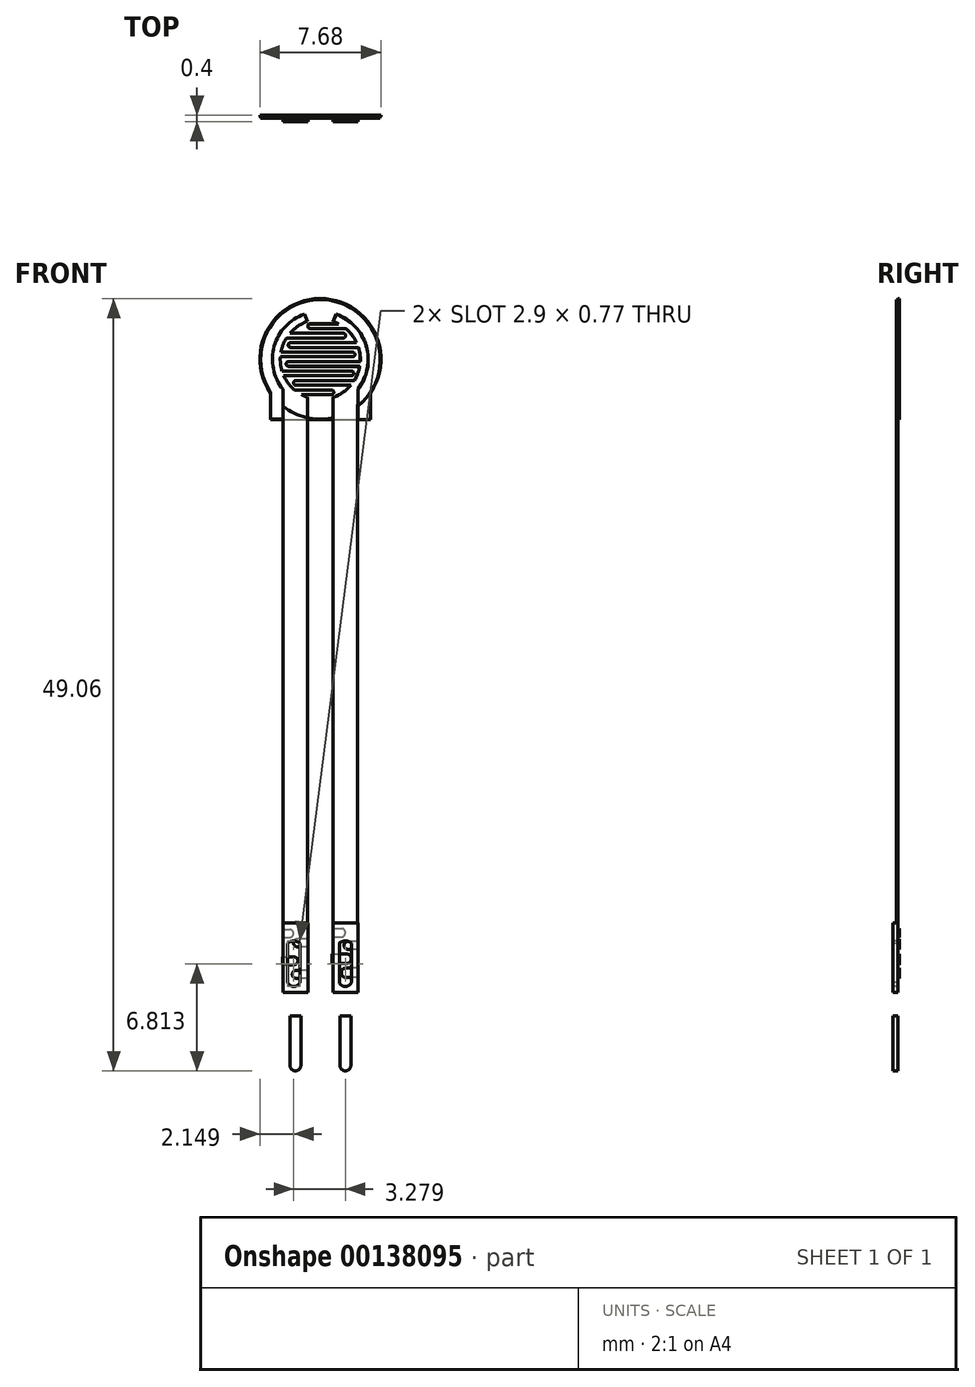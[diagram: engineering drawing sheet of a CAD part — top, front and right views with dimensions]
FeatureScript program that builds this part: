
annotation { "Feature Type Name" : "Feature", "Feature Type Description" : "" }
export const myFeature = defineFeature(function(context is Context, id is Id, definition is map)
    precondition{}
    {
        {
            var Q0;
            Q0=qCreatedBy(makeId("Front.planeOp"),FACE);
            var sketch = newSketch(context, id + "F0", { "sketchPlane" : qUnion([Q0])});
            skCircle(sketch, "E0", {"center": v(0, 37.21) * mm, "radius": 3.8 * mm});
            skLineSegment(sketch, "E1", {"start": v(-3.18, 35.12) * mm, "end": v(-3.18, -2.98) * mm});
            skLineSegment(sketch, "E2", {"start": v(-3.18, -2.98) * mm, "end": v(3.17, -2.98) * mm});
            skLineSegment(sketch, "E3", {"start": v(3.18, -2.98) * mm, "end": v(3.17, 35.12) * mm});
            skArc(sketch, "E4", {"start": v(0.8, 34.8) * mm, "mid": v(1.42, 35.1) * mm, "end": v(1.94, 35.57) * mm});
            skLineSegment(sketch, "E5", {"start": v(3.17, 33.4) * mm, "end": v(-3.18, 33.42) * mm});
            skLineSegment(sketch, "E6", {"start": v(3.17, 28.36) * mm, "end": v(2.42, 28.36) * mm, "construction": true});
            skLineSegment(sketch, "E7", {"start": v(2.42, 28.36) * mm, "end": v(2.42, 27.61) * mm, "construction": true});
            skLineSegment(sketch, "E8", {"start": v(2.42, 27.61) * mm, "end": v(3.17, 27.61) * mm, "construction": true});
            skLineSegment(sketch, "E9", {"start": v(-3.18, 28.38) * mm, "end": v(-2.42, 28.38) * mm, "construction": true});
            skLineSegment(sketch, "E10", {"start": v(-2.42, 28.38) * mm, "end": v(-2.42, 27.63) * mm, "construction": true});
            skLineSegment(sketch, "E11", {"start": v(-2.42, 27.63) * mm, "end": v(-3.17, 27.63) * mm, "construction": true});
            skLineSegment(sketch, "E12", {"start": v(-3.17, 3.52) * mm, "end": v(3.18, 3.52) * mm, "construction": true});
            skLineSegment(sketch, "E13.bottom", {"start": v(-2.38, 1.42) * mm, "end": v(-0.8, 1.42) * mm});
            skLineSegment(sketch, "E13.top", {"start": v(-2.38, -4.48) * mm, "end": v(-0.8, -4.48) * mm});
            skLineSegment(sketch, "E13.left", {"start": v(-2.38, 1.42) * mm, "end": v(-2.38, -4.48) * mm});
            skLineSegment(sketch, "E13.right", {"start": v(-0.8, 1.42) * mm, "end": v(-0.8, -4.48) * mm});
            skLineSegment(sketch, "E14.bottom", {"start": v(0.8, 1.42) * mm, "end": v(2.38, 1.42) * mm});
            skLineSegment(sketch, "E14.top", {"start": v(0.8, -4.48) * mm, "end": v(2.38, -4.48) * mm});
            skLineSegment(sketch, "E14.left", {"start": v(0.8, 1.42) * mm, "end": v(0.8, -4.48) * mm});
            skLineSegment(sketch, "E14.right", {"start": v(2.38, 1.42) * mm, "end": v(2.38, -4.48) * mm});
            skLineSegment(sketch, "E15", {"start": v(-1.94, -4.48) * mm, "end": v(-1.94, -7.63) * mm});
            skLineSegment(sketch, "E16", {"start": v(-1.94, -7.63) * mm, "end": v(-1.24, -7.63) * mm, "construction": true});
            skLineSegment(sketch, "E17", {"start": v(-1.24, -7.63) * mm, "end": v(-1.24, -4.48) * mm});
            skLineSegment(sketch, "E18", {"start": v(-1.24, -4.48) * mm, "end": v(-1.94, -4.48) * mm});
            skLineSegment(sketch, "E19", {"start": v(1.24, -4.48) * mm, "end": v(1.24, -7.63) * mm});
            skLineSegment(sketch, "E20", {"start": v(1.24, -7.63) * mm, "end": v(1.94, -7.63) * mm, "construction": true});
            skLineSegment(sketch, "E21", {"start": v(1.94, -7.63) * mm, "end": v(1.94, -4.48) * mm});
            skLineSegment(sketch, "E22", {"start": v(1.94, -4.48) * mm, "end": v(1.24, -4.48) * mm});
            skArc(sketch, "E23", {"start": v(1.24, -7.63) * mm, "mid": v(1.59, -7.98) * mm, "end": v(1.94, -7.63) * mm});
            skArc(sketch, "E24", {"start": v(-1.94, -7.63) * mm, "mid": v(-1.59, -7.98) * mm, "end": v(-1.24, -7.63) * mm});
            skLineSegment(sketch, "E25", {"start": v(-1.59, -7.63) * mm, "end": v(-1.59, -7.98) * mm, "construction": true});
            skLineSegment(sketch, "E26", {"start": v(1.59, -7.63) * mm, "end": v(1.59, -7.98) * mm, "construction": true});
            skLineSegment(sketch, "E27", {"start": v(0.8, 1.42) * mm, "end": v(0.8, 33.41) * mm, "construction": true});
            skLineSegment(sketch, "E28", {"start": v(0.8, 33.41) * mm, "end": v(2.38, 33.4) * mm});
            skLineSegment(sketch, "E29", {"start": v(2.38, 33.4) * mm, "end": v(2.38, 1.42) * mm, "construction": true});
            skLineSegment(sketch, "E30", {"start": v(-0.8, 1.42) * mm, "end": v(-0.8, 33.42) * mm, "construction": true});
            skLineSegment(sketch, "E31", {"start": v(-0.8, 33.42) * mm, "end": v(-2.38, 33.42) * mm});
            skLineSegment(sketch, "E32", {"start": v(-2.38, 33.42) * mm, "end": v(-2.38, 1.42) * mm, "construction": true});
            skArc(sketch, "E33.0", {"start": v(2.38, 35.33) * mm, "mid": v(2.92, 38.06) * mm, "end": v(1.01, 40.08) * mm});
            skLineSegment(sketch, "E34", {"start": v(-2.38, 33.42) * mm, "end": v(-2.38, 35.32) * mm});
            skLineSegment(sketch, "E35", {"start": v(-0.8, 33.42) * mm, "end": v(-0.8, 34.28) * mm});
            skLineSegment(sketch, "E36", {"start": v(0.8, 33.41) * mm, "end": v(0.8, 34.28) * mm});
            skLineSegment(sketch, "E37", {"start": v(2.38, 33.4) * mm, "end": v(2.38, 35.33) * mm});
            skLineSegment(sketch, "E38", {"start": v(-0.8, 34.28) * mm, "end": v(-0.8, 34.8) * mm});
            skLineSegment(sketch, "E39", {"start": v(0.8, 34.28) * mm, "end": v(0.8, 34.8) * mm});
            skArc(sketch, "E40.trimOffspring", {"start": v(-1.01, 40.08) * mm, "mid": v(-2.92, 38.05) * mm, "end": v(-2.38, 35.32) * mm});
            skArc(sketch, "E41.trimOffspring", {"start": v(-0.8, 39.62) * mm, "mid": v(-1.41, 39.33) * mm, "end": v(-1.92, 38.87) * mm});
            skLineSegment(sketch, "E42", {"start": v(-0.8, 39.62) * mm, "end": v(-1.01, 40.08) * mm, "construction": true});
            skLineSegment(sketch, "E43", {"start": v(0.8, 39.62) * mm, "end": v(1.01, 40.08) * mm});
            skLineSegment(sketch, "E44", {"start": v(1.16, 39.47) * mm, "end": v(-0.64, 39.47) * mm});
            skLineSegment(sketch, "E45", {"start": v(-0.64, 39.17) * mm, "end": v(1.61, 39.17) * mm});
            skLineSegment(sketch, "E46", {"start": v(-1.92, 38.87) * mm, "end": v(1.46, 38.87) * mm});
            skLineSegment(sketch, "E47", {"start": v(1.46, 38.57) * mm, "end": v(-2.14, 38.57) * mm});
            skLineSegment(sketch, "E48", {"start": v(2.3, 38.27) * mm, "end": v(-1.88, 38.27) * mm});
            skLineSegment(sketch, "E49", {"start": v(-1.88, 37.97) * mm, "end": v(2.42, 37.97) * mm});
            skLineSegment(sketch, "E50", {"start": v(-2.5, 37.67) * mm, "end": v(2.05, 37.67) * mm});
            skLineSegment(sketch, "E51", {"start": v(2.05, 37.37) * mm, "end": v(-2.53, 37.37) * mm});
            skLineSegment(sketch, "E52", {"start": v(2.54, 37.07) * mm, "end": v(-2.02, 37.07) * mm});
            skLineSegment(sketch, "E53", {"start": v(-2.02, 36.77) * mm, "end": v(2.5, 36.77) * mm});
            skLineSegment(sketch, "E54", {"start": v(-2.43, 36.47) * mm, "end": v(1.98, 36.47) * mm});
            skLineSegment(sketch, "E55", {"start": v(1.98, 36.17) * mm, "end": v(-2.32, 36.17) * mm});
            skLineSegment(sketch, "E56", {"start": v(2.16, 35.87) * mm, "end": v(-1.55, 35.87) * mm});
            skLineSegment(sketch, "E57", {"start": v(-1.55, 35.57) * mm, "end": v(1.94, 35.57) * mm});
            skLineSegment(sketch, "E58", {"start": v(-1.64, 35.27) * mm, "end": v(0.71, 35.27) * mm});
            skLineSegment(sketch, "E59", {"start": v(0.71, 34.97) * mm, "end": v(-1.2, 34.97) * mm});
            skArc(sketch, "E60", {"start": v(-0.64, 39.47) * mm, "mid": v(-0.79, 39.32) * mm, "end": v(-0.64, 39.17) * mm});
            skArc(sketch, "E61", {"start": v(1.46, 38.57) * mm, "mid": v(1.61, 38.72) * mm, "end": v(1.46, 38.87) * mm});
            skArc(sketch, "E62", {"start": v(-1.88, 38.27) * mm, "mid": v(-2.03, 38.12) * mm, "end": v(-1.88, 37.97) * mm});
            skArc(sketch, "E63", {"start": v(2.05, 37.37) * mm, "mid": v(2.2, 37.52) * mm, "end": v(2.05, 37.67) * mm});
            skArc(sketch, "E64", {"start": v(-2.02, 37.07) * mm, "mid": v(-2.17, 36.92) * mm, "end": v(-2.02, 36.77) * mm});
            skArc(sketch, "E65", {"start": v(1.98, 36.17) * mm, "mid": v(2.13, 36.32) * mm, "end": v(1.98, 36.47) * mm});
            skArc(sketch, "E66", {"start": v(-1.55, 35.87) * mm, "mid": v(-1.7, 35.72) * mm, "end": v(-1.55, 35.57) * mm});
            skArc(sketch, "E67", {"start": v(0.71, 34.97) * mm, "mid": v(0.86, 35.12) * mm, "end": v(0.71, 35.27) * mm});
            skArc(sketch, "E68.trimOffspring", {"start": v(1.16, 39.47) * mm, "mid": v(0.98, 39.56) * mm, "end": v(0.8, 39.62) * mm});
            skArc(sketch, "E69.trimOffspring", {"start": v(2.3, 38.27) * mm, "mid": v(2.01, 38.76) * mm, "end": v(1.61, 39.17) * mm});
            skArc(sketch, "E70.trimOffspring", {"start": v(2.54, 37.07) * mm, "mid": v(2.52, 37.53) * mm, "end": v(2.42, 37.97) * mm});
            skArc(sketch, "E71.trimOffspring", {"start": v(2.16, 35.87) * mm, "mid": v(2.37, 36.3) * mm, "end": v(2.5, 36.77) * mm});
            skArc(sketch, "E72.trimOffspring", {"start": v(-1.2, 34.97) * mm, "mid": v(-1, 34.88) * mm, "end": v(-0.8, 34.8) * mm});
            skArc(sketch, "E73.trimOffspring", {"start": v(-2.32, 36.17) * mm, "mid": v(-2.03, 35.69) * mm, "end": v(-1.64, 35.27) * mm});
            skArc(sketch, "E74.trimOffspring", {"start": v(-2.53, 37.37) * mm, "mid": v(-2.52, 36.92) * mm, "end": v(-2.43, 36.47) * mm});
            skArc(sketch, "E75.trimOffspring", {"start": v(-2.14, 38.57) * mm, "mid": v(-2.36, 38.14) * mm, "end": v(-2.5, 37.67) * mm});
            skLineSegment(sketch, "E76", {"start": v(3.17, 35.12) * mm, "end": v(3.17, 33.4) * mm});
            skLineSegment(sketch, "E77", {"start": v(-3.18, 35.12) * mm, "end": v(-3.18, 33.42) * mm, "construction": true});
            skSolve(sketch);
        }
        {
            var Q0;
            {var subQ5=sQuery(id+"F0.wireOp",EDGE,"E1");Q0=makeQuery(id+"F0.imprint","IMPRINT",FACE,{"disambiguationData":[TD([[makeQuery(id+"F0.imprint","IMPRINT",EDGE,{"derivedFrom":subQ5}),1.0]])]});}
            var sketch = newSketch(context, id + "F1", { "sketchPlane" : qUnion([Q0])});
            skArc(sketch, "E78", {"start": v(0.79, 34.8) * mm, "mid": v(1.41, 35.12) * mm, "end": v(1.93, 35.58) * mm});
            skLineSegment(sketch, "E79", {"start": v(3.12, 28.36) * mm, "end": v(2.37, 28.36) * mm});
            skLineSegment(sketch, "E80", {"start": v(2.37, 28.36) * mm, "end": v(2.37, 27.61) * mm, "construction": true});
            skLineSegment(sketch, "E81", {"start": v(2.37, 27.61) * mm, "end": v(3.12, 27.61) * mm});
            skLineSegment(sketch, "E82", {"start": v(-3.14, 28.38) * mm, "end": v(-2.39, 28.38) * mm});
            skLineSegment(sketch, "E83", {"start": v(-2.39, 28.38) * mm, "end": v(-2.39, 27.63) * mm, "construction": true});
            skLineSegment(sketch, "E84", {"start": v(-2.39, 27.63) * mm, "end": v(-3.14, 27.63) * mm});
            skLineSegment(sketch, "E85.bottom", {"start": v(-2.39, 1.43) * mm, "end": v(-0.8, 1.43) * mm});
            skLineSegment(sketch, "E86.bottom", {"start": v(0.79, 1.43) * mm, "end": v(2.37, 1.43) * mm});
            skLineSegment(sketch, "E87", {"start": v(0.79, 1.43) * mm, "end": v(0.79, 33.42) * mm});
            skLineSegment(sketch, "E88", {"start": v(2.37, 33.41) * mm, "end": v(2.37, 1.43) * mm});
            skLineSegment(sketch, "E89", {"start": v(-0.8, 1.43) * mm, "end": v(-0.8, 33.42) * mm});
            skLineSegment(sketch, "E90", {"start": v(-2.39, 33.43) * mm, "end": v(-2.39, 1.43) * mm});
            skArc(sketch, "E91.0", {"start": v(2.38, 35.33) * mm, "mid": v(2.91, 38.06) * mm, "end": v(1, 40.09) * mm});
            skLineSegment(sketch, "E92", {"start": v(-2.39, 33.43) * mm, "end": v(-2.39, 35.33) * mm});
            skLineSegment(sketch, "E93", {"start": v(-0.8, 33.42) * mm, "end": v(-0.8, 34.29) * mm});
            skLineSegment(sketch, "E94", {"start": v(0.79, 33.42) * mm, "end": v(0.79, 34.29) * mm});
            skLineSegment(sketch, "E95", {"start": v(2.37, 33.41) * mm, "end": v(2.38, 35.33) * mm});
            skLineSegment(sketch, "E96", {"start": v(-0.8, 34.29) * mm, "end": v(-0.8, 34.8) * mm});
            skLineSegment(sketch, "E97", {"start": v(0.79, 34.29) * mm, "end": v(0.79, 34.8) * mm});
            skArc(sketch, "E98.trimOffspring", {"start": v(-1.02, 40.09) * mm, "mid": v(-2.93, 38.06) * mm, "end": v(-2.39, 35.33) * mm});
            skArc(sketch, "E99.trimOffspring", {"start": v(-0.8, 39.63) * mm, "mid": v(-1.42, 39.33) * mm, "end": v(-1.93, 38.88) * mm});
            skLineSegment(sketch, "E100", {"start": v(-0.8, 39.63) * mm, "end": v(-1.02, 40.09) * mm});
            skLineSegment(sketch, "E101", {"start": v(0.79, 39.63) * mm, "end": v(1, 40.09) * mm});
            skLineSegment(sketch, "E102", {"start": v(1.15, 39.48) * mm, "end": v(-0.64, 39.48) * mm});
            skLineSegment(sketch, "E103", {"start": v(-0.64, 39.18) * mm, "end": v(1.6, 39.18) * mm});
            skLineSegment(sketch, "E104", {"start": v(-1.93, 38.88) * mm, "end": v(1.46, 38.88) * mm});
            skLineSegment(sketch, "E105", {"start": v(1.46, 38.58) * mm, "end": v(-2.15, 38.58) * mm});
            skLineSegment(sketch, "E106", {"start": v(2.3, 38.28) * mm, "end": v(-1.9, 38.28) * mm});
            skLineSegment(sketch, "E107", {"start": v(-1.9, 37.98) * mm, "end": v(2.42, 37.98) * mm});
            skLineSegment(sketch, "E108", {"start": v(-2.5, 37.68) * mm, "end": v(2.05, 37.68) * mm});
            skLineSegment(sketch, "E109", {"start": v(2.05, 37.38) * mm, "end": v(-2.54, 37.38) * mm});
            skLineSegment(sketch, "E110", {"start": v(2.53, 37.08) * mm, "end": v(-2.02, 37.08) * mm});
            skLineSegment(sketch, "E111", {"start": v(-2.02, 36.78) * mm, "end": v(2.5, 36.78) * mm});
            skLineSegment(sketch, "E112", {"start": v(-2.44, 36.48) * mm, "end": v(1.97, 36.48) * mm});
            skLineSegment(sketch, "E113", {"start": v(1.97, 36.18) * mm, "end": v(-2.33, 36.18) * mm});
            skLineSegment(sketch, "E114", {"start": v(2.15, 35.88) * mm, "end": v(-1.55, 35.88) * mm});
            skLineSegment(sketch, "E115", {"start": v(-1.55, 35.58) * mm, "end": v(1.93, 35.58) * mm});
            skLineSegment(sketch, "E116", {"start": v(-1.65, 35.28) * mm, "end": v(0.7, 35.28) * mm});
            skLineSegment(sketch, "E117", {"start": v(0.7, 34.98) * mm, "end": v(-1.2, 34.98) * mm});
            skArc(sketch, "E118", {"start": v(-0.64, 39.48) * mm, "mid": v(-0.8, 39.33) * mm, "end": v(-0.64, 39.18) * mm});
            skArc(sketch, "E119", {"start": v(1.46, 38.58) * mm, "mid": v(1.6, 38.73) * mm, "end": v(1.46, 38.88) * mm});
            skArc(sketch, "E120", {"start": v(-1.9, 38.28) * mm, "mid": v(-2.04, 38.13) * mm, "end": v(-1.9, 37.98) * mm});
            skArc(sketch, "E121", {"start": v(2.05, 37.38) * mm, "mid": v(2.2, 37.53) * mm, "end": v(2.05, 37.68) * mm});
            skArc(sketch, "E122", {"start": v(-2.02, 37.08) * mm, "mid": v(-2.17, 36.93) * mm, "end": v(-2.02, 36.78) * mm});
            skArc(sketch, "E123", {"start": v(1.97, 36.18) * mm, "mid": v(2.12, 36.33) * mm, "end": v(1.97, 36.48) * mm});
            skArc(sketch, "E124", {"start": v(-1.55, 35.88) * mm, "mid": v(-1.7, 35.73) * mm, "end": v(-1.55, 35.58) * mm});
            skArc(sketch, "E125", {"start": v(0.7, 34.98) * mm, "mid": v(0.85, 35.13) * mm, "end": v(0.7, 35.28) * mm});
            skArc(sketch, "E126.trimOffspring", {"start": v(1.15, 39.48) * mm, "mid": v(0.97, 39.56) * mm, "end": v(0.79, 39.63) * mm});
            skArc(sketch, "E127.trimOffspring", {"start": v(2.3, 38.28) * mm, "mid": v(2, 38.77) * mm, "end": v(1.6, 39.18) * mm});
            skArc(sketch, "E128.trimOffspring", {"start": v(2.53, 37.08) * mm, "mid": v(2.51, 37.54) * mm, "end": v(2.42, 37.98) * mm});
            skArc(sketch, "E129.trimOffspring", {"start": v(2.15, 35.88) * mm, "mid": v(2.37, 36.32) * mm, "end": v(2.5, 36.78) * mm});
            skArc(sketch, "E130.trimOffspring", {"start": v(-1.2, 34.98) * mm, "mid": v(-1.01, 34.89) * mm, "end": v(-0.8, 34.8) * mm});
            skArc(sketch, "E131.trimOffspring", {"start": v(-2.33, 36.18) * mm, "mid": v(-2.04, 35.7) * mm, "end": v(-1.65, 35.28) * mm});
            skArc(sketch, "E132.trimOffspring", {"start": v(-2.54, 37.38) * mm, "mid": v(-2.53, 36.93) * mm, "end": v(-2.44, 36.48) * mm});
            skArc(sketch, "E133.trimOffspring", {"start": v(-2.15, 38.58) * mm, "mid": v(-2.37, 38.15) * mm, "end": v(-2.5, 37.68) * mm});
            skPoint(sketch, "E134.orphan", {"position": v(3.17, 33.4) * mm});
            skPoint(sketch, "E135.trimOffspring.end.orphan", {"position": v(-3.18, 33.42) * mm});
            skLineSegment(sketch, "E136", {"start": v(3.12, 28.36) * mm, "end": v(3.12, 27.61) * mm});
            skLineSegment(sketch, "E137", {"start": v(-3.14, 28.38) * mm, "end": v(-3.14, 27.63) * mm});
            skLineSegment(sketch, "E138", {"start": v(-3.18, 33.42) * mm, "end": v(-3.14, 28.38) * mm});
            skLineSegment(sketch, "E139", {"start": v(-3.18, 33.42) * mm, "end": v(-2.39, 33.43) * mm});
            skLineSegment(sketch, "E140", {"start": v(2.37, 33.41) * mm, "end": v(3.17, 33.4) * mm});
            skLineSegment(sketch, "E141", {"start": v(3.12, 28.36) * mm, "end": v(3.17, 33.4) * mm});
            skLineSegment(sketch, "E142", {"start": v(3.12, 27.61) * mm, "end": v(3.12, -2.98) * mm});
            skLineSegment(sketch, "E143", {"start": v(3.12, -2.98) * mm, "end": v(2.37, -2.98) * mm});
            skLineSegment(sketch, "E144", {"start": v(2.37, -2.98) * mm, "end": v(2.37, 1.43) * mm});
            skLineSegment(sketch, "E145", {"start": v(-0.8, 1.43) * mm, "end": v(-0.8, -2.97) * mm});
            skLineSegment(sketch, "E146", {"start": v(-0.8, -2.97) * mm, "end": v(0.8, -2.97) * mm});
            skLineSegment(sketch, "E147", {"start": v(0.8, -2.97) * mm, "end": v(0.79, 1.43) * mm});
            skLineSegment(sketch, "E148", {"start": v(-2.39, 1.43) * mm, "end": v(-2.39, -2.98) * mm});
            skLineSegment(sketch, "E149", {"start": v(-2.39, -2.98) * mm, "end": v(-3.18, -2.98) * mm});
            skLineSegment(sketch, "E150", {"start": v(-3.18, -2.98) * mm, "end": v(-3.14, 27.63) * mm});
            skLineSegment(sketch, "E151.bottom", {"start": v(2.37, 28.36) * mm, "end": v(3.12, 28.36) * mm});
            skLineSegment(sketch, "E151.left", {"start": v(2.37, 28.36) * mm, "end": v(2.37, 27.61) * mm});
            skLineSegment(sketch, "E152.bottom", {"start": v(-2.39, 28.38) * mm, "end": v(-3.14, 28.38) * mm});
            skLineSegment(sketch, "E152.left", {"start": v(-2.39, 28.38) * mm, "end": v(-2.39, 27.63) * mm});
            skSolve(sketch);
        }
        {
            var Q0;
            {var subQ3=sQuery(id+"F1.wireOp",EDGE,"E85.bottom");Q0=makeQuery(id+"F1.imprint","IMPRINT",FACE,{"disambiguationData":[TD([[makeQuery(id+"F1.imprint","IMPRINT",EDGE,{"derivedFrom":subQ3}),1.0]])]});}
            var Q1;
            Q1=makeQuery(id+"F1.imprint","IMPRINT",FACE,{"disambiguationData":[TD([[makeQuery(id+"F1.imprint","IMPRINT",EDGE,{"derivedFrom":sQuery(id+"F1.wireOp",EDGE,"E78")}),-1.0]])]});
            extrude(context, id + "F2", {"entities" : qUnion([Q0, Q1]), "depth" : .1 * mm});
        }
        {
            var Q0;
            Q0=makeQuery(id+"F0.imprint","IMPRINT",FACE,{"disambiguationData":[TD([[makeQuery(id+"F0.imprint","IMPRINT",EDGE,{"derivedFrom":sQuery(id+"F0.wireOp",EDGE,"E4")}),1.0]])]});
            var Q1;
            {var subQ0=sQuery(id+"F0.wireOp",EDGE,"E1");var subQ1=sQuery(id+"F0.wireOp",EDGE,"E0");var subQ2=makeQuery(id+"F0.imprint","INTERSECT",VERTEX,{"derivedFrom":[subQ1,subQ0]});Q1=makeQuery(id+"F0.imprint","IMPRINT",FACE,{"disambiguationData":[TD([[makeQuery(id+"F0.imprint","IMPRINT",EDGE,{"disambiguationData":[TD([[subQ2,-1.0]])],"derivedFrom":subQ1}),-1.0]])]});}
            var Q2;
            {var subQ0=sQuery(id+"F0.wireOp",EDGE,"E76");Q2=makeQuery(id+"F0.imprint","IMPRINT",FACE,{"disambiguationData":[TD([[makeQuery(id+"F0.imprint","IMPRINT",EDGE,{"derivedFrom":subQ0}),-1.0]])]});}
            extrude(context, id + "F3", {"entities" : qUnion([Q0, Q1, Q2]), "depth" : .1 * mm});
        }
        {
            var Q0;
            {var subQ5=sQuery(id+"F0.wireOp",EDGE,"E13.bottom");Q0=makeQuery(id+"F0.imprint","IMPRINT",FACE,{"disambiguationData":[TD([[makeQuery(id+"F0.imprint","IMPRINT",EDGE,{"derivedFrom":subQ5}),-1.0]])]});}
            var Q1;
            {var subQ5=sQuery(id+"F0.wireOp",EDGE,"E14.bottom");Q1=makeQuery(id+"F0.imprint","IMPRINT",FACE,{"disambiguationData":[TD([[makeQuery(id+"F0.imprint","IMPRINT",EDGE,{"derivedFrom":subQ5}),-1.0]])]});}
            var Q2;
            {var subQ3=sQuery(id+"F0.wireOp",EDGE,"E18");Q2=makeQuery(id+"F0.imprint","IMPRINT",FACE,{"disambiguationData":[TD([[makeQuery(id+"F0.imprint","IMPRINT",EDGE,{"derivedFrom":subQ3}),-1.0]])]});}
            var Q3;
            {var subQ7=sQuery(id+"F0.wireOp",EDGE,"E22");Q3=makeQuery(id+"F0.imprint","IMPRINT",FACE,{"disambiguationData":[TD([[makeQuery(id+"F0.imprint","IMPRINT",EDGE,{"derivedFrom":subQ7}),-1.0]])]});}
            var Q4;
            Q4=makeQuery(id+"F0.imprint","IMPRINT",FACE,{"disambiguationData":[TD([[makeQuery(id+"F0.imprint","IMPRINT",EDGE,{"derivedFrom":sQuery(id+"F0.wireOp",EDGE,"E15")}),1.0]])]});
            var Q5;
            Q5=makeQuery(id+"F0.imprint","IMPRINT",FACE,{"disambiguationData":[TD([[makeQuery(id+"F0.imprint","IMPRINT",EDGE,{"derivedFrom":sQuery(id+"F0.wireOp",EDGE,"E19")}),1.0]])]});
            extrude(context, id + "F4", {"entities" : qUnion([Q0, Q1, Q2, Q3, Q4, Q5]), "depth" : .3 * mm});
        }
        {
            var Q0;
            {var subQ0=sQuery(id+"F0.wireOp",EDGE,"E35");var subQ1=sQuery(id+"F0.wireOp",EDGE,"E0");var subQ2=makeQuery(id+"F0.imprint","INTERSECT",VERTEX,{"derivedFrom":[subQ1,subQ0]});Q0=makeQuery(id+"F0.imprint","IMPRINT",FACE,{"disambiguationData":[TD([[makeQuery(id+"F0.imprint","IMPRINT",EDGE,{"disambiguationData":[TD([[subQ2,-1.0]])],"derivedFrom":subQ1}),-1.0]])]});}
            var Q1;
            {var subQ0=sQuery(id+"F0.wireOp",EDGE,"E5");var subQ1=sQuery(id+"F0.wireOp",EDGE,"E0");var subQ2=makeQuery(id+"F0.imprint","INTERSECT",VERTEX,{"derivedFrom":[subQ1,subQ0]});Q1=makeQuery(id+"F0.imprint","IMPRINT",FACE,{"disambiguationData":[TD([[makeQuery(id+"F0.imprint","IMPRINT",EDGE,{"disambiguationData":[TD([[subQ2,-1.0]])],"derivedFrom":subQ1}),-1.0]])]});}
            extrude(context, id + "F5", {"entities" : qUnion([Q0, Q1]), "depth" : .1 * mm});
        }
        {
            var Q0;
            {var subQ1=sQuery(id+"F0.wireOp",EDGE,"E3");Q0=makeQuery(id+"F0.imprint","IMPRINT",FACE,{"disambiguationData":[TD([[makeQuery(id+"F0.imprint","IMPRINT",EDGE,{"derivedFrom":subQ1}),1.0]])]});}
            extrude(context, id + "F6", {"entities" : qUnion([Q0]), "depth" : .1 * mm});
        }
        {
            var Q0;
            Q0=makeQuery(id+"F4.opExtrude","CAP_FACE",FACE,{"disambiguationData":[OSD([sQuery(id+"F0.wireOp",EDGE,"E14.bottom"),sQuery(id+"F0.wireOp",EDGE,"E14.top"),sQuery(id+"F0.wireOp",EDGE,"E14.left"),sQuery(id+"F0.wireOp",EDGE,"E14.right"),sQuery(id+"F0.wireOp",EDGE,"E19"),sQuery(id+"F0.wireOp",EDGE,"E21"),sQuery(id+"F0.wireOp",EDGE,"E23")])],"isStart":false});
            var sketch = newSketch(context, id + "F7", { "sketchPlane" : qUnion([Q0])});
            skLineSegment(sketch, "E153", {"start": v(1.59, 1.42) * mm, "end": v(1.59, -4.05) * mm, "construction": true});
            skLineSegment(sketch, "E154", {"start": v(-1.7, 1.12) * mm, "end": v(-1.7, -4.3) * mm, "construction": true});
            skLineSegment(sketch, "E155.bottom", {"start": v(-1.3, 0.14) * mm, "end": v(-2.08, 0.14) * mm});
            skLineSegment(sketch, "E155.top", {"start": v(-1.3, -2.36) * mm, "end": v(-2.08, -2.36) * mm});
            skLineSegment(sketch, "E155.left", {"start": v(-1.3, 0.14) * mm, "end": v(-1.3, -2.36) * mm});
            skLineSegment(sketch, "E155.right", {"start": v(-2.08, 0.14) * mm, "end": v(-2.08, -2.36) * mm});
            skPoint(sketch, "E155.middle", {"position": v(-1.7, -1.11) * mm});
            skLineSegment(sketch, "E156.bottom", {"start": v(1.97, 0.14) * mm, "end": v(1.2, 0.14) * mm});
            skLineSegment(sketch, "E156.top", {"start": v(1.97, -2.36) * mm, "end": v(1.2, -2.36) * mm});
            skLineSegment(sketch, "E156.left", {"start": v(1.97, 0.14) * mm, "end": v(1.97, -2.36) * mm});
            skLineSegment(sketch, "E156.right", {"start": v(1.2, 0.14) * mm, "end": v(1.2, -2.36) * mm});
            skPoint(sketch, "E156.middle", {"position": v(1.59, -1.11) * mm});
            skLineSegment(sketch, "E157", {"start": v(-1.3, 0.14) * mm, "end": v(1.2, 0.14) * mm, "construction": true});
            skArc(sketch, "E158", {"start": v(-1.3, 0.14) * mm, "mid": v(-1.7, 0.28) * mm, "end": v(-2.08, 0.14) * mm});
            skArc(sketch, "E159", {"start": v(-2.08, -2.36) * mm, "mid": v(-1.7, -2.62) * mm, "end": v(-1.3, -2.36) * mm});
            skArc(sketch, "E160", {"start": v(1.97, 0.14) * mm, "mid": v(1.59, 0.28) * mm, "end": v(1.2, 0.14) * mm});
            skArc(sketch, "E161", {"start": v(1.2, -2.36) * mm, "mid": v(1.59, -2.62) * mm, "end": v(1.97, -2.36) * mm});
            skSolve(sketch);
        }
        {
            var Q0;
            Q0 = qSketchRegion(id + "F7", true);
            extrude(context, id + "F8", {"entities" : qUnion([Q0]), "operationType" : NewBodyOperationType.REMOVE, "oppositeDirection" : true, "depth" : .5 * mm});
        }
        {
            var Q0;
            {var subQ5=sQuery(id+"F0.wireOp",EDGE,"E13.bottom");Q0=makeQuery(id+"F0.imprint","IMPRINT",FACE,{"disambiguationData":[TD([[makeQuery(id+"F0.imprint","IMPRINT",EDGE,{"derivedFrom":subQ5}),-1.0]])]});}
            var sketch = newSketch(context, id + "F9", { "sketchPlane" : qUnion([Q0])});
            skLineSegment(sketch, "E162.bottom", {"start": v(-2.37, 1) * mm, "end": v(-1.96, 1) * mm});
            skLineSegment(sketch, "E162.top", {"start": v(-2.37, 0.5) * mm, "end": v(-1.96, 0.5) * mm});
            skLineSegment(sketch, "E162.left", {"start": v(-2.37, 1) * mm, "end": v(-2.37, 0.5) * mm});
            skLineSegment(sketch, "E163.bottom", {"start": v(-0.78, 0.4) * mm, "end": v(-1.46, 0.4) * mm});
            skLineSegment(sketch, "E163.top", {"start": v(-0.78, -0.1) * mm, "end": v(-1.46, -0.1) * mm});
            skLineSegment(sketch, "E163.left", {"start": v(-0.78, 0.4) * mm, "end": v(-0.78, -0.1) * mm});
            skLineSegment(sketch, "E164.bottom", {"start": v(-2.4, -0.74) * mm, "end": v(-1.68, -0.74) * mm});
            skLineSegment(sketch, "E164.top", {"start": v(-2.4, -1.24) * mm, "end": v(-1.68, -1.24) * mm});
            skLineSegment(sketch, "E164.left", {"start": v(-2.4, -0.74) * mm, "end": v(-2.4, -1.24) * mm});
            skLineSegment(sketch, "E165.bottom", {"start": v(-0.78, -1.6) * mm, "end": v(-1.54, -1.6) * mm});
            skLineSegment(sketch, "E165.top", {"start": v(-0.78, -2.1) * mm, "end": v(-1.54, -2.1) * mm});
            skLineSegment(sketch, "E165.left", {"start": v(-0.78, -1.6) * mm, "end": v(-0.78, -2.1) * mm});
            skLineSegment(sketch, "E166.bottom", {"start": v(0.82, 1.08) * mm, "end": v(1.4, 1.08) * mm});
            skLineSegment(sketch, "E166.top", {"start": v(0.82, 0.54) * mm, "end": v(1.4, 0.54) * mm});
            skLineSegment(sketch, "E166.left", {"start": v(0.82, 1.08) * mm, "end": v(0.82, 0.54) * mm});
            skLineSegment(sketch, "E167.bottom", {"start": v(2.38, 0.25) * mm, "end": v(1.76, 0.25) * mm});
            skLineSegment(sketch, "E167.top", {"start": v(2.38, -0.25) * mm, "end": v(1.76, -0.25) * mm});
            skLineSegment(sketch, "E167.left", {"start": v(2.38, 0.25) * mm, "end": v(2.38, -0.25) * mm});
            skLineSegment(sketch, "E168.bottom", {"start": v(0.75, -0.55) * mm, "end": v(1.66, -0.55) * mm});
            skLineSegment(sketch, "E168.top", {"start": v(0.75, -1.15) * mm, "end": v(1.66, -1.15) * mm});
            skLineSegment(sketch, "E168.left", {"start": v(0.75, -0.55) * mm, "end": v(0.75, -1.15) * mm});
            skLineSegment(sketch, "E169.bottom", {"start": v(2.37, -1.45) * mm, "end": v(1.63, -1.45) * mm});
            skLineSegment(sketch, "E169.top", {"start": v(2.37, -2.04) * mm, "end": v(1.63, -2.04) * mm});
            skLineSegment(sketch, "E169.left", {"start": v(2.37, -1.45) * mm, "end": v(2.37, -2.04) * mm});
            skArc(sketch, "E170", {"start": v(1.4, 0.54) * mm, "mid": v(1.59, 0.8) * mm, "end": v(1.4, 1.08) * mm});
            skArc(sketch, "E171", {"start": v(1.66, -1.15) * mm, "mid": v(1.96, -0.85) * mm, "end": v(1.66, -0.55) * mm});
            skArc(sketch, "E172", {"start": v(1.63, -1.45) * mm, "mid": v(1.33, -1.74) * mm, "end": v(1.63, -2.04) * mm});
            skArc(sketch, "E173", {"start": v(-1.54, -1.6) * mm, "mid": v(-1.79, -1.84) * mm, "end": v(-1.54, -2.1) * mm});
            skArc(sketch, "E174", {"start": v(-1.68, -1.24) * mm, "mid": v(-1.43, -0.99) * mm, "end": v(-1.68, -0.74) * mm});
            skArc(sketch, "E175", {"start": v(-1.46, 0.4) * mm, "mid": v(-1.7, 0.15) * mm, "end": v(-1.46, -0.1) * mm});
            skArc(sketch, "E176", {"start": v(-1.96, 0.5) * mm, "mid": v(-1.7, 0.76) * mm, "end": v(-1.96, 1) * mm});
            skArc(sketch, "E177", {"start": v(1.76, 0.25) * mm, "mid": v(1.5, 0) * mm, "end": v(1.76, -0.25) * mm});
            skSolve(sketch);
        }
        {
            var Q0;
            Q0 = qSketchRegion(id + "F9", true);
            extrude(context, id + "F10", {"entities" : qUnion([Q0]), "oppositeDirection" : true, "depth" : .1 * mm});
        }
        {
            var Q0;
            Q0=makeQuery(id+"F0.imprint","IMPRINT",FACE,{"disambiguationData":[TD([[makeQuery(id+"F0.imprint","IMPRINT",EDGE,{"derivedFrom":sQuery(id+"F0.wireOp",EDGE,"E4")}),1.0]])]});
            var sketch = newSketch(context, id + "F11", { "sketchPlane" : qUnion([Q0])});
            skCircle(sketch, "E178", {"center": v(0, 37.24) * mm, "radius": 3.84 * mm});
            skLineSegment(sketch, "E179", {"start": v(-3.17, 35.07) * mm, "end": v(-3.17, 33.4) * mm});
            skLineSegment(sketch, "E180", {"start": v(-3.17, 33.4) * mm, "end": v(3.2, 33.4) * mm});
            skLineSegment(sketch, "E181", {"start": v(3.2, 33.4) * mm, "end": v(3.2, 35.11) * mm});
            skSolve(sketch);
        }
        {
            var Q0;
            Q0 = qSketchRegion(id + "F11", true);
            extrude(context, id + "F12", {"entities" : qUnion([Q0]), "oppositeDirection" : true, "depth" : .1 * mm});
        }
    });
